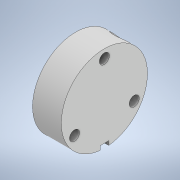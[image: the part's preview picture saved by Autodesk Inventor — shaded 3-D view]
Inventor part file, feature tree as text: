
AUTODESK INVENTOR PART (.ipt)
format: ipt  version: 2022 (Build 260153000, 153)  size: 166,912 bytes
history: native  units: mm
features: sketch x5, other x2, revolve x2, hole x2, extrude x1
ambient origin geometry x8: Origin, YZ Plane, XZ Plane, XY Plane, X Axis, Y Axis, Z Axis, Center Point
bodies: Body1 (feature_tree)
feature tree (12):
  other  "Твердое тело1"
  revolve  "Вращение1"
  hole  "Отверстие1"  [1 undecoded]
  hole  "Отверстие2"  [1 undecoded]
  extrude  "Выдавливание1"  TaperAngle=360.0deg  [1 undecoded]
  other  "РабПлоскость1"
  revolve  "Вращение3"
  sketch  "Эскиз1"
  sketch  "Эскиз2"
  sketch  "Эскиз3"
  sketch  "Эскиз4"
  sketch  "Эскиз5"
note: 3 required parameter values undecoded (feature->parameter linkage not recoverable at this tier; creation-order binding heuristic only, values carry confidence <= 0.55)
